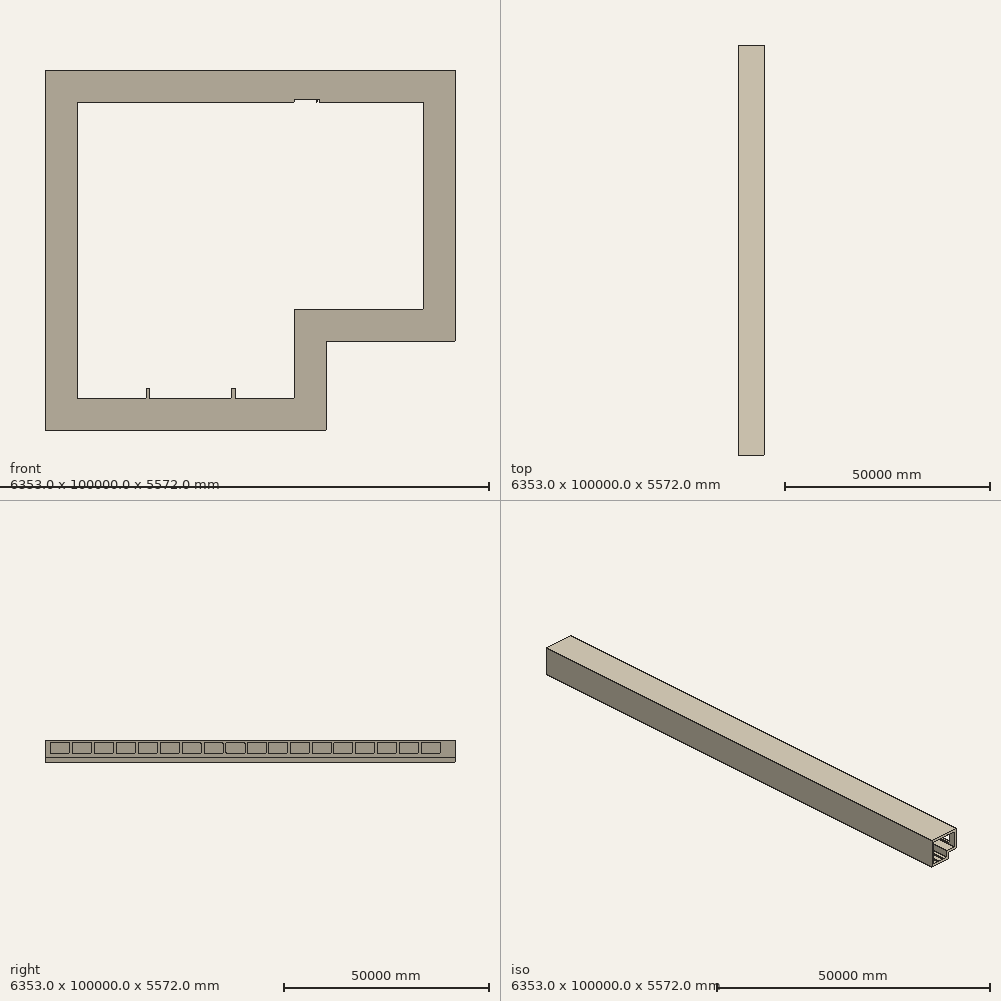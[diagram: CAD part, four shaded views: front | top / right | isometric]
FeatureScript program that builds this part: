
annotation { "Feature Type Name" : "Feature", "Feature Type Description" : "" }
export const myFeature = defineFeature(function(context is Context, id is Id, definition is map)
    precondition{}
    {
        {
            var Q0;
            Q0=qCreatedBy(makeId("Front.planeOp"),FACE);
            var sketch = newSketch(context, id + "F0", { "sketchPlane" : qUnion([Q0])});
            skLineSegment(sketch, "E0", {"start": v(0, 0) * mm, "end": v(2000, 0) * mm});
            skLineSegment(sketch, "E1", {"start": v(2000, 0) * mm, "end": v(2000, 3201) * mm});
            skLineSegment(sketch, "E2", {"start": v(2000, 3201) * mm, "end": v(400, 3201) * mm});
            skLineSegment(sketch, "E3", {"start": v(-3353, 3201) * mm, "end": v(-3353, -1371) * mm});
            skLineSegment(sketch, "E4", {"start": v(-3353, -1371) * mm, "end": v(-2285, -1371) * mm});
            skLineSegment(sketch, "E5", {"start": v(0, -1371) * mm, "end": v(0, 0) * mm});
            skLineSegment(sketch, "E6.0", {"start": v(-3853, -1871) * mm, "end": v(500, -1871) * mm});
            skLineSegment(sketch, "E7.0", {"start": v(500, -1871) * mm, "end": v(500, -500) * mm});
            skLineSegment(sketch, "E8.0", {"start": v(500, -500) * mm, "end": v(2500, -500) * mm});
            skLineSegment(sketch, "E9.0", {"start": v(2500, -500) * mm, "end": v(2500, 3701) * mm});
            skLineSegment(sketch, "E10.0", {"start": v(-3853, 3701) * mm, "end": v(-3853, -1871) * mm});
            skLineSegment(sketch, "E11.0", {"start": v(2500, 3701) * mm, "end": v(-3853, 3701) * mm});
            skLineSegment(sketch, "E12", {"start": v(-2285, -1219) * mm, "end": v(-2235, -1219) * mm});
            skLineSegment(sketch, "E13", {"start": v(-1600, -1371) * mm, "end": v(-1600, -768.26) * mm, "construction": true});
            skLineSegment(sketch, "E14.0", {"start": v(-965, -1371) * mm, "end": v(-965, -1219) * mm});
            skLineSegment(sketch, "E15.0", {"start": v(-2235, -1371) * mm, "end": v(-2235, -1219) * mm});
            skLineSegment(sketch, "E16.0", {"start": v(-915, -1371) * mm, "end": v(-915, -1219) * mm});
            skLineSegment(sketch, "E17.0", {"start": v(-2285, -1371) * mm, "end": v(-2285, -1219) * mm});
            skLineSegment(sketch, "E18", {"start": v(-1792.5, -1219) * mm, "end": v(-1600, -1219) * mm});
            skLineSegment(sketch, "E19.trimOffspring", {"start": v(-965, -1219) * mm, "end": v(-915, -1219) * mm});
            skLineSegment(sketch, "E20.trimOffspring", {"start": v(-915, -1371) * mm, "end": v(0, -1371) * mm});
            skLineSegment(sketch, "E21.trimOffspring", {"start": v(-2235, -1371) * mm, "end": v(-965, -1371) * mm});
            skLineSegment(sketch, "E22", {"start": v(0, 3201) * mm, "end": v(0, 3251) * mm});
            skLineSegment(sketch, "E23", {"start": v(0, 3251) * mm, "end": v(140, 3251) * mm});
            skLineSegment(sketch, "E24", {"start": v(400, 3251) * mm, "end": v(400, 3201) * mm});
            skLineSegment(sketch, "E25.trimOffspring", {"start": v(0, 3201) * mm, "end": v(-3353, 3201) * mm});
            skLineSegment(sketch, "E26.0", {"start": v(140, 3201) * mm, "end": v(140, 3251) * mm});
            skLineSegment(sketch, "E27.0", {"start": v(350, 3201) * mm, "end": v(350, 3251) * mm});
            skLineSegment(sketch, "E28.0", {"start": v(145, 3251) * mm, "end": v(145, 3272.73) * mm});
            skLineSegment(sketch, "E29.0", {"start": v(355, 3212.24) * mm, "end": v(355, 3251) * mm});
            skLineSegment(sketch, "E30.trimOffspring", {"start": v(145, 3251) * mm, "end": v(350, 3251) * mm});
            skLineSegment(sketch, "E31.trimOffspring", {"start": v(355, 3251) * mm, "end": v(400, 3251) * mm});
            skLineSegment(sketch, "E32", {"start": v(140, 3201) * mm, "end": v(145, 3272.73) * mm});
            skLineSegment(sketch, "E33", {"start": v(350, 3201) * mm, "end": v(355, 3212.24) * mm});
            skSolve(sketch);
        }
        {
            var Q0;
            Q0 = qSketchRegion(id + "F0", true);
            extrude(context, id + "F1", {"entities" : qUnion([Q0]), "depth" : 100000 * mm, "offsetDistance" : 25 * mm});
        }
        {
            var Q0;
            Q0=makeQuery(id+"F1.opExtrude","SWEPT_FACE",FACE,{"disambiguationData":[OSD([sQuery(id+"F0.wireOp",EDGE,"E9.0")])]});
            var sketch = newSketch(context, id + "F2", { "sketchPlane" : qUnion([Q0])});
            skLineSegment(sketch, "E34.bottom", {"start": v(-98529.65, 357.35) * mm, "end": v(-94385.73, 357.35) * mm});
            skLineSegment(sketch, "E34.top", {"start": v(-98529.65, 3128) * mm, "end": v(-94385.73, 3128) * mm});
            skLineSegment(sketch, "E34.left", {"start": v(-98779.65, 607.35) * mm, "end": v(-98779.65, 2878) * mm});
            skLineSegment(sketch, "E34.right", {"start": v(-94135.73, 607.35) * mm, "end": v(-94135.73, 2878) * mm});
            skPoint(sketch, "E35.visualSharp", {"position": v(-98779.65, 3128) * mm});
            skArc(sketch, "E35.filletArc", {"start": v(-98529.65, 3128) * mm, "mid": v(-98706.42, 3054.77) * mm, "end": v(-98779.65, 2878) * mm});
            skPoint(sketch, "E36.visualSharp", {"position": v(-94135.73, 3128) * mm});
            skArc(sketch, "E36.filletArc", {"start": v(-94135.73, 2878) * mm, "mid": v(-94208.95, 3054.77) * mm, "end": v(-94385.73, 3128) * mm});
            skPoint(sketch, "E37.visualSharp", {"position": v(-94135.73, 357.35) * mm});
            skArc(sketch, "E37.filletArc", {"start": v(-94385.73, 357.35) * mm, "mid": v(-94208.95, 430.57) * mm, "end": v(-94135.73, 607.35) * mm});
            skPoint(sketch, "E38.visualSharp", {"position": v(-98779.65, 357.35) * mm});
            skArc(sketch, "E38.filletArc", {"start": v(-98779.65, 607.35) * mm, "mid": v(-98706.42, 430.57) * mm, "end": v(-98529.65, 357.35) * mm});
            skLineSegment(sketch, "E39.bottom", {"start": v(-93191.93, 357.35) * mm, "end": v(-89048.01, 357.35) * mm});
            skLineSegment(sketch, "E39.top", {"start": v(-93191.93, 3128) * mm, "end": v(-89048.01, 3128) * mm});
            skLineSegment(sketch, "E39.left", {"start": v(-93441.93, 607.35) * mm, "end": v(-93441.93, 2878) * mm});
            skLineSegment(sketch, "E39.right", {"start": v(-88798.01, 607.35) * mm, "end": v(-88798.01, 2878) * mm});
            skPoint(sketch, "E40.visualSharp", {"position": v(-93441.93, 3128) * mm});
            skArc(sketch, "E40.filletArc", {"start": v(-93191.93, 3128) * mm, "mid": v(-93368.7, 3054.77) * mm, "end": v(-93441.93, 2878) * mm});
            skPoint(sketch, "E41.visualSharp", {"position": v(-88798.01, 3128) * mm});
            skArc(sketch, "E41.filletArc", {"start": v(-88798.01, 2878) * mm, "mid": v(-88871.24, 3054.77) * mm, "end": v(-89048.01, 3128) * mm});
            skPoint(sketch, "E42.visualSharp", {"position": v(-88798.01, 357.35) * mm});
            skArc(sketch, "E42.filletArc", {"start": v(-89048.01, 357.35) * mm, "mid": v(-88871.24, 430.57) * mm, "end": v(-88798.01, 607.35) * mm});
            skPoint(sketch, "E43.visualSharp", {"position": v(-93441.93, 357.35) * mm});
            skArc(sketch, "E43.filletArc", {"start": v(-93441.93, 607.35) * mm, "mid": v(-93368.7, 430.57) * mm, "end": v(-93191.93, 357.35) * mm});
            skLineSegment(sketch, "E44.bottom", {"start": v(-87868.01, 357.35) * mm, "end": v(-83724.1, 357.35) * mm});
            skLineSegment(sketch, "E44.top", {"start": v(-87868.01, 3128) * mm, "end": v(-83724.1, 3128) * mm});
            skLineSegment(sketch, "E44.left", {"start": v(-88118.01, 607.35) * mm, "end": v(-88118.01, 2878) * mm});
            skLineSegment(sketch, "E44.right", {"start": v(-83474.1, 607.35) * mm, "end": v(-83474.1, 2878) * mm});
            skPoint(sketch, "E45.visualSharp", {"position": v(-88118.01, 3128) * mm});
            skArc(sketch, "E45.filletArc", {"start": v(-87868.01, 3128) * mm, "mid": v(-88044.79, 3054.77) * mm, "end": v(-88118.01, 2878) * mm});
            skPoint(sketch, "E46.visualSharp", {"position": v(-83474.1, 3128) * mm});
            skArc(sketch, "E46.filletArc", {"start": v(-83474.1, 2878) * mm, "mid": v(-83547.31, 3054.77) * mm, "end": v(-83724.1, 3128) * mm});
            skPoint(sketch, "E47.visualSharp", {"position": v(-83474.1, 357.35) * mm});
            skArc(sketch, "E47.filletArc", {"start": v(-83724.1, 357.35) * mm, "mid": v(-83547.31, 430.57) * mm, "end": v(-83474.1, 607.35) * mm});
            skPoint(sketch, "E48.visualSharp", {"position": v(-88118.01, 357.35) * mm});
            skArc(sketch, "E48.filletArc", {"start": v(-88118.01, 607.35) * mm, "mid": v(-88044.79, 430.57) * mm, "end": v(-87868.01, 357.35) * mm});
            skLineSegment(sketch, "E49.bottom", {"start": v(-82454.09, 357.35) * mm, "end": v(-78310.17, 357.35) * mm});
            skLineSegment(sketch, "E49.top", {"start": v(-82454.09, 3128) * mm, "end": v(-78310.17, 3128) * mm});
            skLineSegment(sketch, "E49.left", {"start": v(-82704.09, 607.35) * mm, "end": v(-82704.09, 2878) * mm});
            skLineSegment(sketch, "E49.right", {"start": v(-78060.17, 607.35) * mm, "end": v(-78060.17, 2878) * mm});
            skPoint(sketch, "E50.visualSharp", {"position": v(-82704.09, 3128) * mm});
            skArc(sketch, "E50.filletArc", {"start": v(-82454.09, 3128) * mm, "mid": v(-82630.86, 3054.77) * mm, "end": v(-82704.09, 2878) * mm});
            skPoint(sketch, "E51.visualSharp", {"position": v(-78060.17, 3128) * mm});
            skArc(sketch, "E51.filletArc", {"start": v(-78060.17, 2878) * mm, "mid": v(-78133.39, 3054.77) * mm, "end": v(-78310.17, 3128) * mm});
            skPoint(sketch, "E52.visualSharp", {"position": v(-78060.17, 357.35) * mm});
            skArc(sketch, "E52.filletArc", {"start": v(-78310.17, 357.35) * mm, "mid": v(-78133.39, 430.57) * mm, "end": v(-78060.17, 607.35) * mm});
            skPoint(sketch, "E53.visualSharp", {"position": v(-82704.09, 357.35) * mm});
            skArc(sketch, "E53.filletArc", {"start": v(-82704.09, 607.35) * mm, "mid": v(-82630.86, 430.57) * mm, "end": v(-82454.09, 357.35) * mm});
            skLineSegment(sketch, "E54.bottom", {"start": v(-77120.16, 357.35) * mm, "end": v(-72976.24, 357.35) * mm});
            skLineSegment(sketch, "E54.top", {"start": v(-77120.16, 3128) * mm, "end": v(-72976.24, 3128) * mm});
            skLineSegment(sketch, "E54.left", {"start": v(-77370.16, 607.35) * mm, "end": v(-77370.16, 2878) * mm});
            skLineSegment(sketch, "E54.right", {"start": v(-72726.24, 607.35) * mm, "end": v(-72726.24, 2878) * mm});
            skPoint(sketch, "E55.visualSharp", {"position": v(-77370.16, 3128) * mm});
            skArc(sketch, "E55.filletArc", {"start": v(-77120.16, 3128) * mm, "mid": v(-77296.94, 3054.77) * mm, "end": v(-77370.16, 2878) * mm});
            skPoint(sketch, "E56.visualSharp", {"position": v(-72726.24, 3128) * mm});
            skArc(sketch, "E56.filletArc", {"start": v(-72726.24, 2878) * mm, "mid": v(-72799.47, 3054.77) * mm, "end": v(-72976.24, 3128) * mm});
            skPoint(sketch, "E57.visualSharp", {"position": v(-72726.24, 357.35) * mm});
            skArc(sketch, "E57.filletArc", {"start": v(-72976.24, 357.35) * mm, "mid": v(-72799.47, 430.57) * mm, "end": v(-72726.24, 607.35) * mm});
            skPoint(sketch, "E58.visualSharp", {"position": v(-77370.16, 357.35) * mm});
            skArc(sketch, "E58.filletArc", {"start": v(-77370.16, 607.35) * mm, "mid": v(-77296.94, 430.57) * mm, "end": v(-77120.16, 357.35) * mm});
            skLineSegment(sketch, "E59.bottom", {"start": v(-71756.24, 357.35) * mm, "end": v(-67612.32, 357.35) * mm});
            skLineSegment(sketch, "E59.top", {"start": v(-71756.24, 3128) * mm, "end": v(-67612.32, 3128) * mm});
            skLineSegment(sketch, "E59.left", {"start": v(-72006.24, 607.35) * mm, "end": v(-72006.24, 2878) * mm});
            skLineSegment(sketch, "E59.right", {"start": v(-67362.32, 607.35) * mm, "end": v(-67362.32, 2878) * mm});
            skPoint(sketch, "E60.visualSharp", {"position": v(-72006.24, 3128) * mm});
            skArc(sketch, "E60.filletArc", {"start": v(-71756.24, 3128) * mm, "mid": v(-71933.02, 3054.77) * mm, "end": v(-72006.24, 2878) * mm});
            skPoint(sketch, "E61.visualSharp", {"position": v(-67362.32, 3128) * mm});
            skArc(sketch, "E61.filletArc", {"start": v(-67362.32, 2878) * mm, "mid": v(-67435.54, 3054.77) * mm, "end": v(-67612.32, 3128) * mm});
            skPoint(sketch, "E62.visualSharp", {"position": v(-67362.32, 357.35) * mm});
            skArc(sketch, "E62.filletArc", {"start": v(-67612.32, 357.35) * mm, "mid": v(-67435.54, 430.57) * mm, "end": v(-67362.32, 607.35) * mm});
            skPoint(sketch, "E63.visualSharp", {"position": v(-72006.24, 357.35) * mm});
            skArc(sketch, "E63.filletArc", {"start": v(-72006.24, 607.35) * mm, "mid": v(-71933.02, 430.57) * mm, "end": v(-71756.24, 357.35) * mm});
            skLineSegment(sketch, "E64.bottom", {"start": v(-66452.32, 357.35) * mm, "end": v(-62308.4, 357.35) * mm});
            skLineSegment(sketch, "E64.top", {"start": v(-66452.32, 3128) * mm, "end": v(-62308.4, 3128) * mm});
            skLineSegment(sketch, "E64.left", {"start": v(-66702.32, 607.35) * mm, "end": v(-66702.32, 2878) * mm});
            skLineSegment(sketch, "E64.right", {"start": v(-62058.4, 607.35) * mm, "end": v(-62058.4, 2878) * mm});
            skPoint(sketch, "E65.visualSharp", {"position": v(-66702.32, 3128) * mm});
            skArc(sketch, "E65.filletArc", {"start": v(-66452.32, 3128) * mm, "mid": v(-66629.1, 3054.77) * mm, "end": v(-66702.32, 2878) * mm});
            skPoint(sketch, "E66.visualSharp", {"position": v(-62058.4, 3128) * mm});
            skArc(sketch, "E66.filletArc", {"start": v(-62058.4, 2878) * mm, "mid": v(-62131.62, 3054.77) * mm, "end": v(-62308.4, 3128) * mm});
            skPoint(sketch, "E67.visualSharp", {"position": v(-62058.4, 357.35) * mm});
            skArc(sketch, "E67.filletArc", {"start": v(-62308.4, 357.35) * mm, "mid": v(-62131.62, 430.57) * mm, "end": v(-62058.4, 607.35) * mm});
            skPoint(sketch, "E68.visualSharp", {"position": v(-66702.32, 357.35) * mm});
            skArc(sketch, "E68.filletArc", {"start": v(-66702.32, 607.35) * mm, "mid": v(-66629.1, 430.57) * mm, "end": v(-66452.32, 357.35) * mm});
            skLineSegment(sketch, "E69.bottom", {"start": v(-61080.88, 357.35) * mm, "end": v(-56936.96, 357.35) * mm});
            skLineSegment(sketch, "E69.top", {"start": v(-61080.88, 3128) * mm, "end": v(-56936.96, 3128) * mm});
            skLineSegment(sketch, "E69.left", {"start": v(-61330.88, 607.35) * mm, "end": v(-61330.88, 2878) * mm});
            skLineSegment(sketch, "E69.right", {"start": v(-56686.96, 607.35) * mm, "end": v(-56686.96, 2878) * mm});
            skPoint(sketch, "E70.visualSharp", {"position": v(-61330.88, 3128) * mm});
            skArc(sketch, "E70.filletArc", {"start": v(-61080.88, 3128) * mm, "mid": v(-61257.66, 3054.77) * mm, "end": v(-61330.88, 2878) * mm});
            skPoint(sketch, "E71.visualSharp", {"position": v(-56686.96, 3128) * mm});
            skArc(sketch, "E71.filletArc", {"start": v(-56686.96, 2878) * mm, "mid": v(-56760.19, 3054.77) * mm, "end": v(-56936.96, 3128) * mm});
            skPoint(sketch, "E72.visualSharp", {"position": v(-56686.96, 357.35) * mm});
            skArc(sketch, "E72.filletArc", {"start": v(-56936.96, 357.35) * mm, "mid": v(-56760.19, 430.57) * mm, "end": v(-56686.96, 607.35) * mm});
            skPoint(sketch, "E73.visualSharp", {"position": v(-61330.88, 357.35) * mm});
            skArc(sketch, "E73.filletArc", {"start": v(-61330.88, 607.35) * mm, "mid": v(-61257.66, 430.57) * mm, "end": v(-61080.88, 357.35) * mm});
            skLineSegment(sketch, "E74.bottom", {"start": v(-55726.98, 357.35) * mm, "end": v(-51583.06, 357.35) * mm});
            skLineSegment(sketch, "E74.top", {"start": v(-55726.98, 3128) * mm, "end": v(-51583.06, 3128) * mm});
            skLineSegment(sketch, "E74.left", {"start": v(-55976.98, 607.35) * mm, "end": v(-55976.98, 2878) * mm});
            skLineSegment(sketch, "E74.right", {"start": v(-51333.06, 607.35) * mm, "end": v(-51333.06, 2878) * mm});
            skPoint(sketch, "E75.visualSharp", {"position": v(-55976.98, 3128) * mm});
            skArc(sketch, "E75.filletArc", {"start": v(-55726.98, 3128) * mm, "mid": v(-55903.76, 3054.77) * mm, "end": v(-55976.98, 2878) * mm});
            skPoint(sketch, "E76.visualSharp", {"position": v(-51333.06, 3128) * mm});
            skArc(sketch, "E76.filletArc", {"start": v(-51333.06, 2878) * mm, "mid": v(-51406.28, 3054.77) * mm, "end": v(-51583.06, 3128) * mm});
            skPoint(sketch, "E77.visualSharp", {"position": v(-51333.06, 357.35) * mm});
            skArc(sketch, "E77.filletArc", {"start": v(-51583.06, 357.35) * mm, "mid": v(-51406.28, 430.57) * mm, "end": v(-51333.06, 607.35) * mm});
            skPoint(sketch, "E78.visualSharp", {"position": v(-55976.98, 357.35) * mm});
            skArc(sketch, "E78.filletArc", {"start": v(-55976.98, 607.35) * mm, "mid": v(-55903.76, 430.57) * mm, "end": v(-55726.98, 357.35) * mm});
            skLineSegment(sketch, "E79.bottom", {"start": v(-50529.13, 357.35) * mm, "end": v(-46385.2, 357.35) * mm});
            skLineSegment(sketch, "E79.top", {"start": v(-50529.13, 3128) * mm, "end": v(-46385.2, 3128) * mm});
            skLineSegment(sketch, "E79.left", {"start": v(-50779.13, 607.35) * mm, "end": v(-50779.13, 2878) * mm});
            skLineSegment(sketch, "E79.right", {"start": v(-46135.2, 607.35) * mm, "end": v(-46135.2, 2878) * mm});
            skPoint(sketch, "E80.visualSharp", {"position": v(-50779.13, 3128) * mm});
            skArc(sketch, "E80.filletArc", {"start": v(-50529.13, 3128) * mm, "mid": v(-50705.9, 3054.77) * mm, "end": v(-50779.13, 2878) * mm});
            skPoint(sketch, "E81.visualSharp", {"position": v(-46135.2, 3128) * mm});
            skArc(sketch, "E81.filletArc", {"start": v(-46135.2, 2878) * mm, "mid": v(-46208.43, 3054.77) * mm, "end": v(-46385.2, 3128) * mm});
            skPoint(sketch, "E82.visualSharp", {"position": v(-46135.2, 357.35) * mm});
            skArc(sketch, "E82.filletArc", {"start": v(-46385.2, 357.35) * mm, "mid": v(-46208.43, 430.57) * mm, "end": v(-46135.2, 607.35) * mm});
            skPoint(sketch, "E83.visualSharp", {"position": v(-50779.13, 357.35) * mm});
            skArc(sketch, "E83.filletArc", {"start": v(-50779.13, 607.35) * mm, "mid": v(-50705.9, 430.57) * mm, "end": v(-50529.13, 357.35) * mm});
            skLineSegment(sketch, "E84.bottom", {"start": v(-45305.2, 357.35) * mm, "end": v(-41161.28, 357.35) * mm});
            skLineSegment(sketch, "E84.top", {"start": v(-45305.2, 3128) * mm, "end": v(-41161.28, 3128) * mm});
            skLineSegment(sketch, "E84.left", {"start": v(-45555.2, 607.35) * mm, "end": v(-45555.2, 2878) * mm});
            skLineSegment(sketch, "E84.right", {"start": v(-40911.28, 607.35) * mm, "end": v(-40911.28, 2878) * mm});
            skPoint(sketch, "E85.visualSharp", {"position": v(-45555.2, 3128) * mm});
            skArc(sketch, "E85.filletArc", {"start": v(-45305.2, 3128) * mm, "mid": v(-45481.98, 3054.77) * mm, "end": v(-45555.2, 2878) * mm});
            skPoint(sketch, "E86.visualSharp", {"position": v(-40911.28, 3128) * mm});
            skArc(sketch, "E86.filletArc", {"start": v(-40911.28, 2878) * mm, "mid": v(-40984.5, 3054.77) * mm, "end": v(-41161.28, 3128) * mm});
            skPoint(sketch, "E87.visualSharp", {"position": v(-40911.28, 357.35) * mm});
            skArc(sketch, "E87.filletArc", {"start": v(-41161.28, 357.35) * mm, "mid": v(-40984.5, 430.57) * mm, "end": v(-40911.28, 607.35) * mm});
            skPoint(sketch, "E88.visualSharp", {"position": v(-45555.2, 357.35) * mm});
            skArc(sketch, "E88.filletArc", {"start": v(-45555.2, 607.35) * mm, "mid": v(-45481.98, 430.57) * mm, "end": v(-45305.2, 357.35) * mm});
            skLineSegment(sketch, "E89.bottom", {"start": v(-40033.98, 357.35) * mm, "end": v(-35890.06, 357.35) * mm});
            skLineSegment(sketch, "E89.top", {"start": v(-40033.98, 3128) * mm, "end": v(-35890.06, 3128) * mm});
            skLineSegment(sketch, "E89.left", {"start": v(-40283.98, 607.35) * mm, "end": v(-40283.98, 2878) * mm});
            skLineSegment(sketch, "E89.right", {"start": v(-35640.06, 607.35) * mm, "end": v(-35640.06, 2878) * mm});
            skPoint(sketch, "E90.visualSharp", {"position": v(-40283.98, 3128) * mm});
            skArc(sketch, "E90.filletArc", {"start": v(-40033.98, 3128) * mm, "mid": v(-40210.75, 3054.77) * mm, "end": v(-40283.98, 2878) * mm});
            skPoint(sketch, "E91.visualSharp", {"position": v(-35640.06, 3128) * mm});
            skArc(sketch, "E91.filletArc", {"start": v(-35640.06, 2878) * mm, "mid": v(-35713.28, 3054.77) * mm, "end": v(-35890.06, 3128) * mm});
            skPoint(sketch, "E92.visualSharp", {"position": v(-35640.06, 357.35) * mm});
            skArc(sketch, "E92.filletArc", {"start": v(-35890.06, 357.35) * mm, "mid": v(-35713.28, 430.57) * mm, "end": v(-35640.06, 607.35) * mm});
            skPoint(sketch, "E93.visualSharp", {"position": v(-40283.98, 357.35) * mm});
            skArc(sketch, "E93.filletArc", {"start": v(-40283.98, 607.35) * mm, "mid": v(-40210.75, 430.57) * mm, "end": v(-40033.98, 357.35) * mm});
            skLineSegment(sketch, "E94.bottom", {"start": v(-34680.05, 357.35) * mm, "end": v(-30536.13, 357.35) * mm});
            skLineSegment(sketch, "E94.top", {"start": v(-34680.05, 3128) * mm, "end": v(-30536.13, 3128) * mm});
            skLineSegment(sketch, "E94.left", {"start": v(-34930.05, 607.35) * mm, "end": v(-34930.05, 2878) * mm});
            skLineSegment(sketch, "E94.right", {"start": v(-30286.13, 607.35) * mm, "end": v(-30286.13, 2878) * mm});
            skPoint(sketch, "E95.visualSharp", {"position": v(-34930.05, 3128) * mm});
            skArc(sketch, "E95.filletArc", {"start": v(-34680.05, 3128) * mm, "mid": v(-34856.83, 3054.77) * mm, "end": v(-34930.05, 2878) * mm});
            skPoint(sketch, "E96.visualSharp", {"position": v(-30286.13, 3128) * mm});
            skArc(sketch, "E96.filletArc", {"start": v(-30286.13, 2878) * mm, "mid": v(-30359.36, 3054.77) * mm, "end": v(-30536.13, 3128) * mm});
            skPoint(sketch, "E97.visualSharp", {"position": v(-30286.13, 357.35) * mm});
            skArc(sketch, "E97.filletArc", {"start": v(-30536.13, 357.35) * mm, "mid": v(-30359.36, 430.57) * mm, "end": v(-30286.13, 607.35) * mm});
            skPoint(sketch, "E98.visualSharp", {"position": v(-34930.05, 357.35) * mm});
            skArc(sketch, "E98.filletArc", {"start": v(-34930.05, 607.35) * mm, "mid": v(-34856.83, 430.57) * mm, "end": v(-34680.05, 357.35) * mm});
            skLineSegment(sketch, "E99.bottom", {"start": v(-29396.13, 357.35) * mm, "end": v(-25252.21, 357.35) * mm});
            skLineSegment(sketch, "E99.top", {"start": v(-29396.13, 3128) * mm, "end": v(-25252.21, 3128) * mm});
            skLineSegment(sketch, "E99.left", {"start": v(-29646.13, 607.35) * mm, "end": v(-29646.13, 2878) * mm});
            skLineSegment(sketch, "E99.right", {"start": v(-25002.21, 607.35) * mm, "end": v(-25002.21, 2878) * mm});
            skPoint(sketch, "E100.visualSharp", {"position": v(-29646.13, 3128) * mm});
            skArc(sketch, "E100.filletArc", {"start": v(-29396.13, 3128) * mm, "mid": v(-29572.9, 3054.77) * mm, "end": v(-29646.13, 2878) * mm});
            skPoint(sketch, "E101.visualSharp", {"position": v(-25002.21, 3128) * mm});
            skArc(sketch, "E101.filletArc", {"start": v(-25002.21, 2878) * mm, "mid": v(-25075.43, 3054.77) * mm, "end": v(-25252.21, 3128) * mm});
            skPoint(sketch, "E102.visualSharp", {"position": v(-25002.21, 357.35) * mm});
            skArc(sketch, "E102.filletArc", {"start": v(-25252.21, 357.35) * mm, "mid": v(-25075.43, 430.57) * mm, "end": v(-25002.21, 607.35) * mm});
            skPoint(sketch, "E103.visualSharp", {"position": v(-29646.13, 357.35) * mm});
            skArc(sketch, "E103.filletArc", {"start": v(-29646.13, 607.35) * mm, "mid": v(-29572.9, 430.57) * mm, "end": v(-29396.13, 357.35) * mm});
            skLineSegment(sketch, "E104.bottom", {"start": v(-24062.21, 357.35) * mm, "end": v(-19918.3, 357.35) * mm});
            skLineSegment(sketch, "E104.top", {"start": v(-24062.21, 3128) * mm, "end": v(-19918.3, 3128) * mm});
            skLineSegment(sketch, "E104.left", {"start": v(-24312.21, 607.35) * mm, "end": v(-24312.21, 2878) * mm});
            skLineSegment(sketch, "E104.right", {"start": v(-19668.3, 607.35) * mm, "end": v(-19668.3, 2878) * mm});
            skPoint(sketch, "E105.visualSharp", {"position": v(-24312.21, 3128) * mm});
            skArc(sketch, "E105.filletArc", {"start": v(-24062.21, 3128) * mm, "mid": v(-24238.99, 3054.77) * mm, "end": v(-24312.21, 2878) * mm});
            skPoint(sketch, "E106.visualSharp", {"position": v(-19668.3, 3128) * mm});
            skArc(sketch, "E106.filletArc", {"start": v(-19668.3, 2878) * mm, "mid": v(-19741.51, 3054.77) * mm, "end": v(-19918.3, 3128) * mm});
            skPoint(sketch, "E107.visualSharp", {"position": v(-19668.3, 357.35) * mm});
            skArc(sketch, "E107.filletArc", {"start": v(-19918.3, 357.35) * mm, "mid": v(-19741.51, 430.57) * mm, "end": v(-19668.3, 607.35) * mm});
            skPoint(sketch, "E108.visualSharp", {"position": v(-24312.21, 357.35) * mm});
            skArc(sketch, "E108.filletArc", {"start": v(-24312.21, 607.35) * mm, "mid": v(-24238.99, 430.57) * mm, "end": v(-24062.21, 357.35) * mm});
            skLineSegment(sketch, "E109.bottom", {"start": v(-18698.28, 357.35) * mm, "end": v(-14554.36, 357.35) * mm});
            skLineSegment(sketch, "E109.top", {"start": v(-18698.28, 3128) * mm, "end": v(-14554.36, 3128) * mm});
            skLineSegment(sketch, "E109.left", {"start": v(-18948.28, 607.35) * mm, "end": v(-18948.28, 2878) * mm});
            skLineSegment(sketch, "E109.right", {"start": v(-14304.36, 607.35) * mm, "end": v(-14304.36, 2878) * mm});
            skPoint(sketch, "E110.visualSharp", {"position": v(-18948.28, 3128) * mm});
            skArc(sketch, "E110.filletArc", {"start": v(-18698.28, 3128) * mm, "mid": v(-18875.06, 3054.77) * mm, "end": v(-18948.28, 2878) * mm});
            skPoint(sketch, "E111.visualSharp", {"position": v(-14304.36, 3128) * mm});
            skArc(sketch, "E111.filletArc", {"start": v(-14304.36, 2878) * mm, "mid": v(-14377.58, 3054.77) * mm, "end": v(-14554.36, 3128) * mm});
            skPoint(sketch, "E112.visualSharp", {"position": v(-14304.36, 357.35) * mm});
            skArc(sketch, "E112.filletArc", {"start": v(-14554.36, 357.35) * mm, "mid": v(-14377.58, 430.57) * mm, "end": v(-14304.36, 607.35) * mm});
            skPoint(sketch, "E113.visualSharp", {"position": v(-18948.28, 357.35) * mm});
            skArc(sketch, "E113.filletArc", {"start": v(-18948.28, 607.35) * mm, "mid": v(-18875.06, 430.57) * mm, "end": v(-18698.28, 357.35) * mm});
            skLineSegment(sketch, "E114.bottom", {"start": v(-13324.36, 357.35) * mm, "end": v(-9180.44, 357.35) * mm});
            skLineSegment(sketch, "E114.top", {"start": v(-13324.36, 3128) * mm, "end": v(-9180.44, 3128) * mm});
            skLineSegment(sketch, "E114.left", {"start": v(-13574.36, 607.35) * mm, "end": v(-13574.36, 2878) * mm});
            skLineSegment(sketch, "E114.right", {"start": v(-8930.44, 607.35) * mm, "end": v(-8930.44, 2878) * mm});
            skPoint(sketch, "E115.visualSharp", {"position": v(-13574.36, 3128) * mm});
            skArc(sketch, "E115.filletArc", {"start": v(-13324.36, 3128) * mm, "mid": v(-13501.14, 3054.77) * mm, "end": v(-13574.36, 2878) * mm});
            skPoint(sketch, "E116.visualSharp", {"position": v(-8930.44, 3128) * mm});
            skArc(sketch, "E116.filletArc", {"start": v(-8930.44, 2878) * mm, "mid": v(-9003.66, 3054.77) * mm, "end": v(-9180.44, 3128) * mm});
            skPoint(sketch, "E117.visualSharp", {"position": v(-8930.44, 357.35) * mm});
            skArc(sketch, "E117.filletArc", {"start": v(-9180.44, 357.35) * mm, "mid": v(-9003.66, 430.57) * mm, "end": v(-8930.44, 607.35) * mm});
            skPoint(sketch, "E118.visualSharp", {"position": v(-13574.36, 357.35) * mm});
            skArc(sketch, "E118.filletArc", {"start": v(-13574.36, 607.35) * mm, "mid": v(-13501.14, 430.57) * mm, "end": v(-13324.36, 357.35) * mm});
            skLineSegment(sketch, "E119.bottom", {"start": v(-7980.44, 357.35) * mm, "end": v(-3836.52, 357.35) * mm});
            skLineSegment(sketch, "E119.top", {"start": v(-7980.44, 3128) * mm, "end": v(-3836.52, 3128) * mm});
            skLineSegment(sketch, "E119.left", {"start": v(-8230.44, 607.35) * mm, "end": v(-8230.44, 2878) * mm});
            skLineSegment(sketch, "E119.right", {"start": v(-3586.52, 607.35) * mm, "end": v(-3586.52, 2878) * mm});
            skPoint(sketch, "E120.visualSharp", {"position": v(-8230.44, 3128) * mm});
            skArc(sketch, "E120.filletArc", {"start": v(-7980.44, 3128) * mm, "mid": v(-8157.21, 3054.77) * mm, "end": v(-8230.44, 2878) * mm});
            skPoint(sketch, "E121.visualSharp", {"position": v(-3586.52, 3128) * mm});
            skArc(sketch, "E121.filletArc", {"start": v(-3586.52, 2878) * mm, "mid": v(-3659.74, 3054.77) * mm, "end": v(-3836.52, 3128) * mm});
            skPoint(sketch, "E122.visualSharp", {"position": v(-3586.52, 357.35) * mm});
            skArc(sketch, "E122.filletArc", {"start": v(-3836.52, 357.35) * mm, "mid": v(-3659.74, 430.57) * mm, "end": v(-3586.52, 607.35) * mm});
            skPoint(sketch, "E123.visualSharp", {"position": v(-8230.44, 357.35) * mm});
            skArc(sketch, "E123.filletArc", {"start": v(-8230.44, 607.35) * mm, "mid": v(-8157.21, 430.57) * mm, "end": v(-7980.44, 357.35) * mm});
            skSolve(sketch);
        }
        {
            var Q0;
            Q0 = qSketchRegion(id + "F2", true);
            extrude(context, id + "F3", {"entities" : qUnion([Q0]), "operationType" : NewBodyOperationType.REMOVE, "endBound" : BoundingType.UP_TO_NEXT, "oppositeDirection" : true, "depth" : 25 * mm, "offsetDistance" : 25 * mm});
        }
    });
